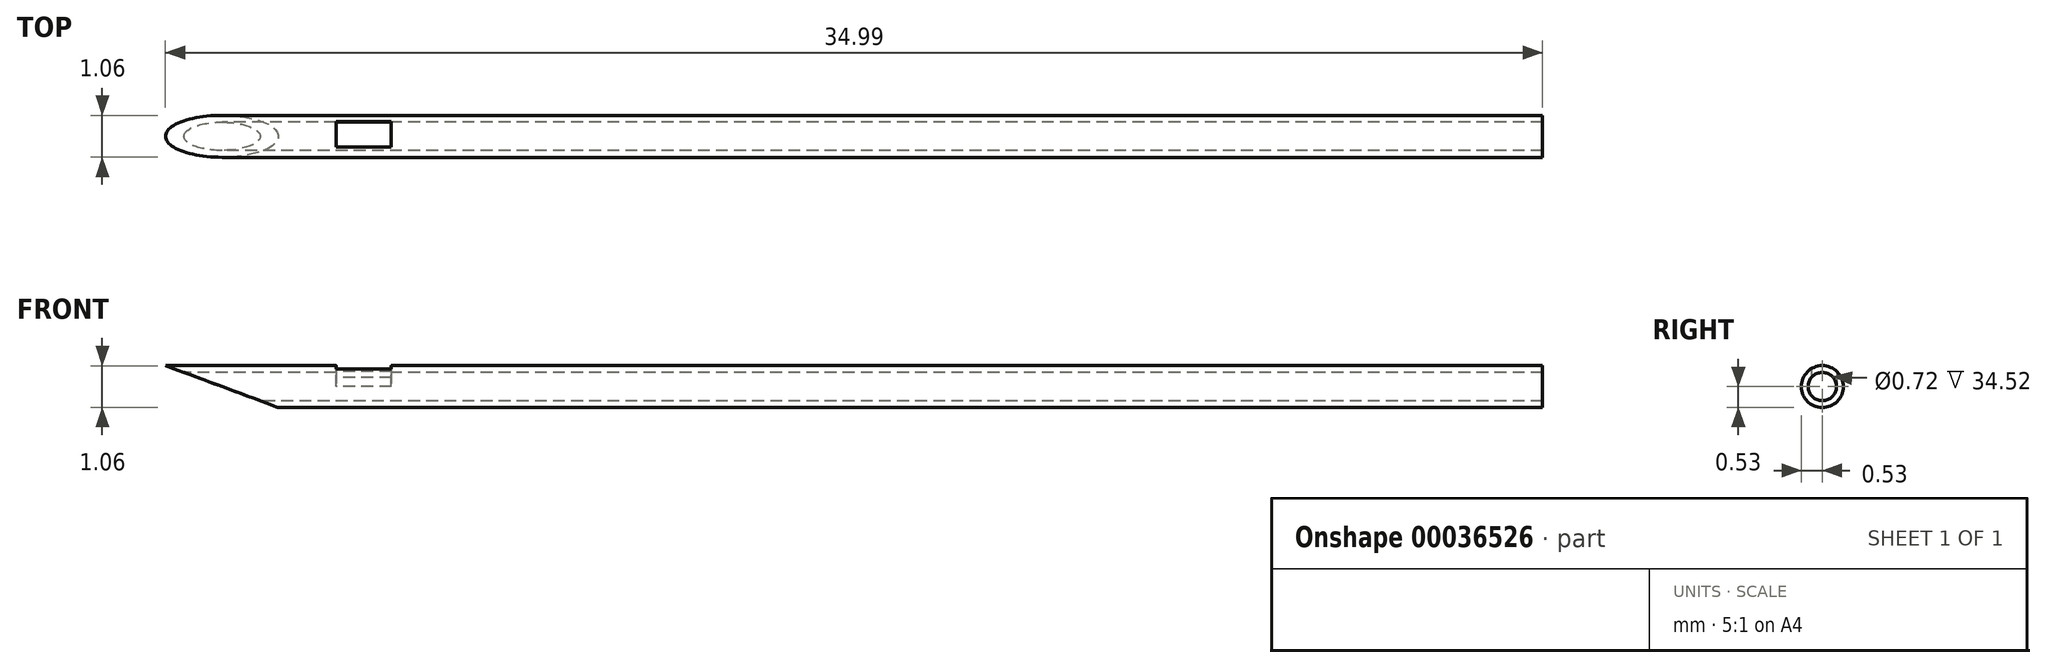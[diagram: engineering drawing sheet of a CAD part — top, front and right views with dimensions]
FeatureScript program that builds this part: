
annotation { "Feature Type Name" : "Feature", "Feature Type Description" : "" }
export const myFeature = defineFeature(function(context is Context, id is Id, definition is map)
    precondition{}
    {
        {
            var Q0;
            Q0=qCreatedBy(makeId("Right.planeOp"),FACE);
            var sketch = newSketch(context, id + "F0", { "sketchPlane" : qUnion([Q0])});
            skCircle(sketch, "E0", {"center": v(0, 0) * mm, "radius": 0.36 * mm});
            skCircle(sketch, "E1", {"center": v(0, 0) * mm, "radius": 0.53 * mm});
            skSolve(sketch);
        }
        {
            var Q0;
            Q0 = qSketchRegion(id + "F0", true);
            extrude(context, id + "F1", {"entities" : qUnion([Q0]), "depth" : 35 * mm});
        }
        {
            var Q0;
            Q0=qCreatedBy(makeId("Front.planeOp"),FACE);
            var sketch = newSketch(context, id + "F2", { "sketchPlane" : qUnion([Q0])});
            skLineSegment(sketch, "E2", {"start": v(0, 0.54) * mm, "end": v(3, -0.57) * mm});
            skLineSegment(sketch, "E3", {"start": v(3, -0.57) * mm, "end": v(0, -0.57) * mm});
            skLineSegment(sketch, "E4", {"start": v(0, -0.57) * mm, "end": v(0, 0.54) * mm});
            skSolve(sketch);
        }
        {
            var Q0;
            Q0 = qSketchRegion(id + "F2", true);
            extrude(context, id + "F3", {"entities" : qUnion([Q0]), "operationType" : NewBodyOperationType.REMOVE, "endBound" : BoundingType.THROUGH_ALL, "oppositeDirection" : true, "depth" : 25 * mm});
        }
        {
            var Q0;
            Q0 = qSketchRegion(id + "F2", true);
            extrude(context, id + "F4", {"entities" : qUnion([Q0]), "operationType" : NewBodyOperationType.REMOVE, "endBound" : BoundingType.THROUGH_ALL, "depth" : 25 * mm});
        }
        {
            var Q0;
            Q0=qCreatedBy(makeId("Top.planeOp"),FACE);
            var sketch = newSketch(context, id + "F5", { "sketchPlane" : qUnion([Q0])});
            skLineSegment(sketch, "E5.bottom", {"start": v(4.35, 0.37) * mm, "end": v(5.75, 0.37) * mm});
            skLineSegment(sketch, "E5.top", {"start": v(4.35, -0.28) * mm, "end": v(5.75, -0.28) * mm});
            skLineSegment(sketch, "E5.left", {"start": v(4.35, 0.37) * mm, "end": v(4.35, -0.28) * mm});
            skLineSegment(sketch, "E5.right", {"start": v(5.75, 0.37) * mm, "end": v(5.75, -0.28) * mm});
            skSolve(sketch);
        }
        {
            var Q0;
            Q0 = qSketchRegion(id + "F5", true);
            extrude(context, id + "F6", {"entities" : qUnion([Q0]), "operationType" : NewBodyOperationType.REMOVE, "depth" : 1 * mm});
        }
    });
